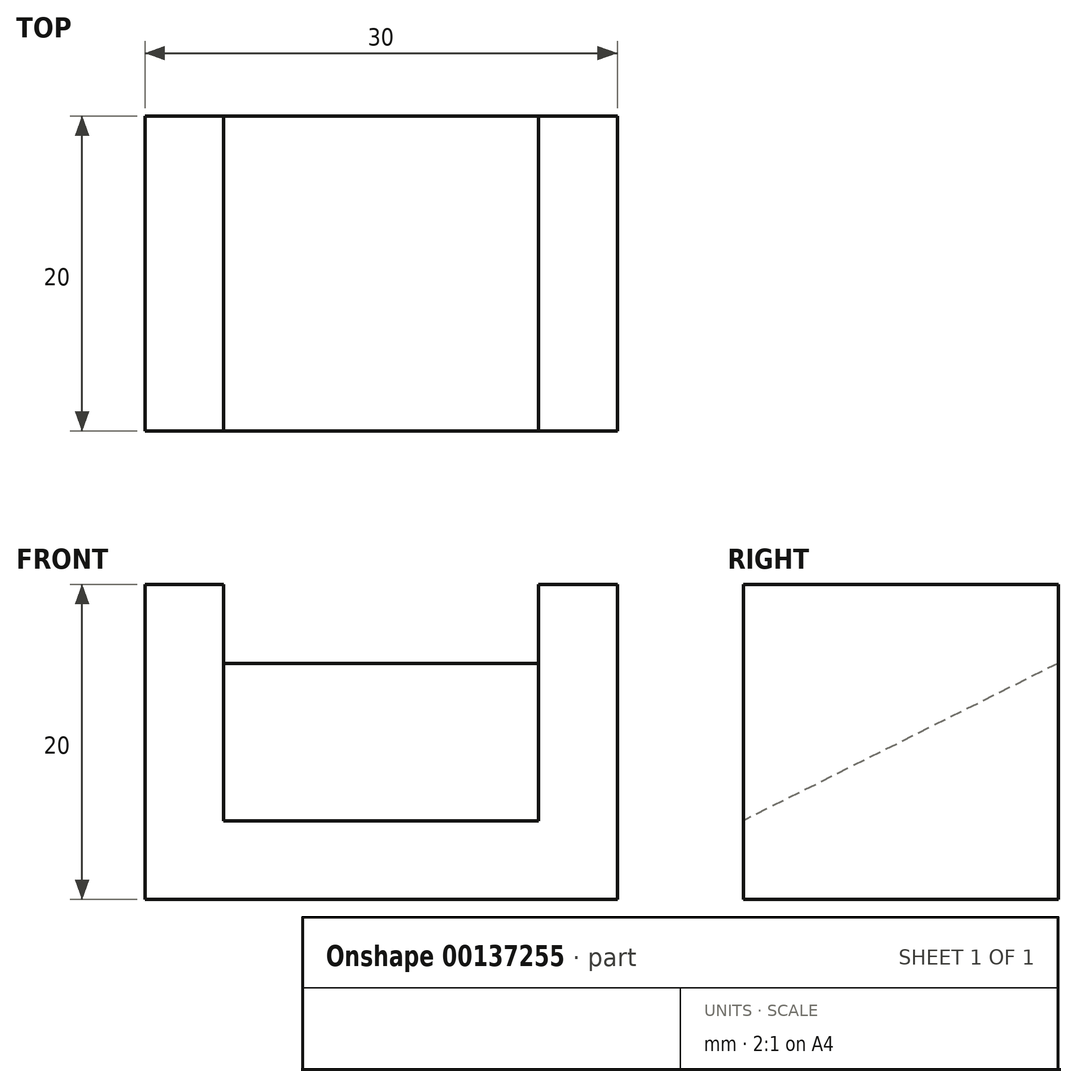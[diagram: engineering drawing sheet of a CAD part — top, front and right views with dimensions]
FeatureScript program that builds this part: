
annotation { "Feature Type Name" : "Feature", "Feature Type Description" : "" }
export const myFeature = defineFeature(function(context is Context, id is Id, definition is map)
    precondition{}
    {
        {
            var Q0;
            Q0=qCreatedBy(makeId("Front.planeOp"),FACE);
            var sketch = newSketch(context, id + "F0", { "sketchPlane" : qUnion([Q0])});
            skLineSegment(sketch, "E0", {"start": v(0, 0) * mm, "end": v(0, 20) * mm});
            skLineSegment(sketch, "E1", {"start": v(0, 20) * mm, "end": v(25, 20) * mm});
            skLineSegment(sketch, "E2", {"start": v(25, 20) * mm, "end": v(25, 0) * mm});
            skLineSegment(sketch, "E3", {"start": v(25, 0) * mm, "end": v(0, 0) * mm});
            skSolve(sketch);
        }
        {
            var Q0;
            Q0 = qSketchRegion(id + "F0", true);
            extrude(context, id + "F1", {"entities" : qUnion([Q0]), "oppositeDirection" : true, "depth" : 20 * mm});
        }
        {
            var Q0;
            Q0=makeQuery(id+"F1.opExtrude","SWEPT_FACE",FACE,{"disambiguationData":[OSD([sQuery(id+"F0.wireOp",EDGE,"E2")])]});
            var sketch = newSketch(context, id + "F2", { "sketchPlane" : qUnion([Q0])});
            skLineSegment(sketch, "E4", {"start": v(20, 15) * mm, "end": v(0, 5) * mm});
            skLineSegment(sketch, "E5", {"start": v(0, 5) * mm, "end": v(0, 20) * mm});
            skLineSegment(sketch, "E6", {"start": v(0, 20) * mm, "end": v(20, 20) * mm});
            skLineSegment(sketch, "E7", {"start": v(20, 20) * mm, "end": v(20, 15) * mm});
            skSolve(sketch);
        }
        {
            var Q0;
            Q0 = qSketchRegion(id + "F2", true);
            extrude(context, id + "F3", {"entities" : qUnion([Q0]), "operationType" : NewBodyOperationType.REMOVE, "oppositeDirection" : true, "depth" : 20 * mm});
        }
        {
            var Q0;
            Q0=makeQuery(id+"F1.opExtrude","SWEPT_FACE",FACE,{"disambiguationData":[OSD([sQuery(id+"F0.wireOp",EDGE,"E2")])]});
            var sketch = newSketch(context, id + "F4", { "sketchPlane" : qUnion([Q0])});
            skLineSegment(sketch, "E8", {"start": v(0, 0) * mm, "end": v(20, 0) * mm});
            skLineSegment(sketch, "E9", {"start": v(20, 0) * mm, "end": v(20, 20) * mm});
            skLineSegment(sketch, "E10", {"start": v(20, 20) * mm, "end": v(0, 20) * mm});
            skLineSegment(sketch, "E11", {"start": v(0, 20) * mm, "end": v(0, 0) * mm});
            skSolve(sketch);
        }
        {
            var Q0;
            Q0 = qSketchRegion(id + "F4", true);
            extrude(context, id + "F5", {"entities" : qUnion([Q0]), "operationType" : NewBodyOperationType.ADD, "depth" : 5 * mm});
        }
    });
